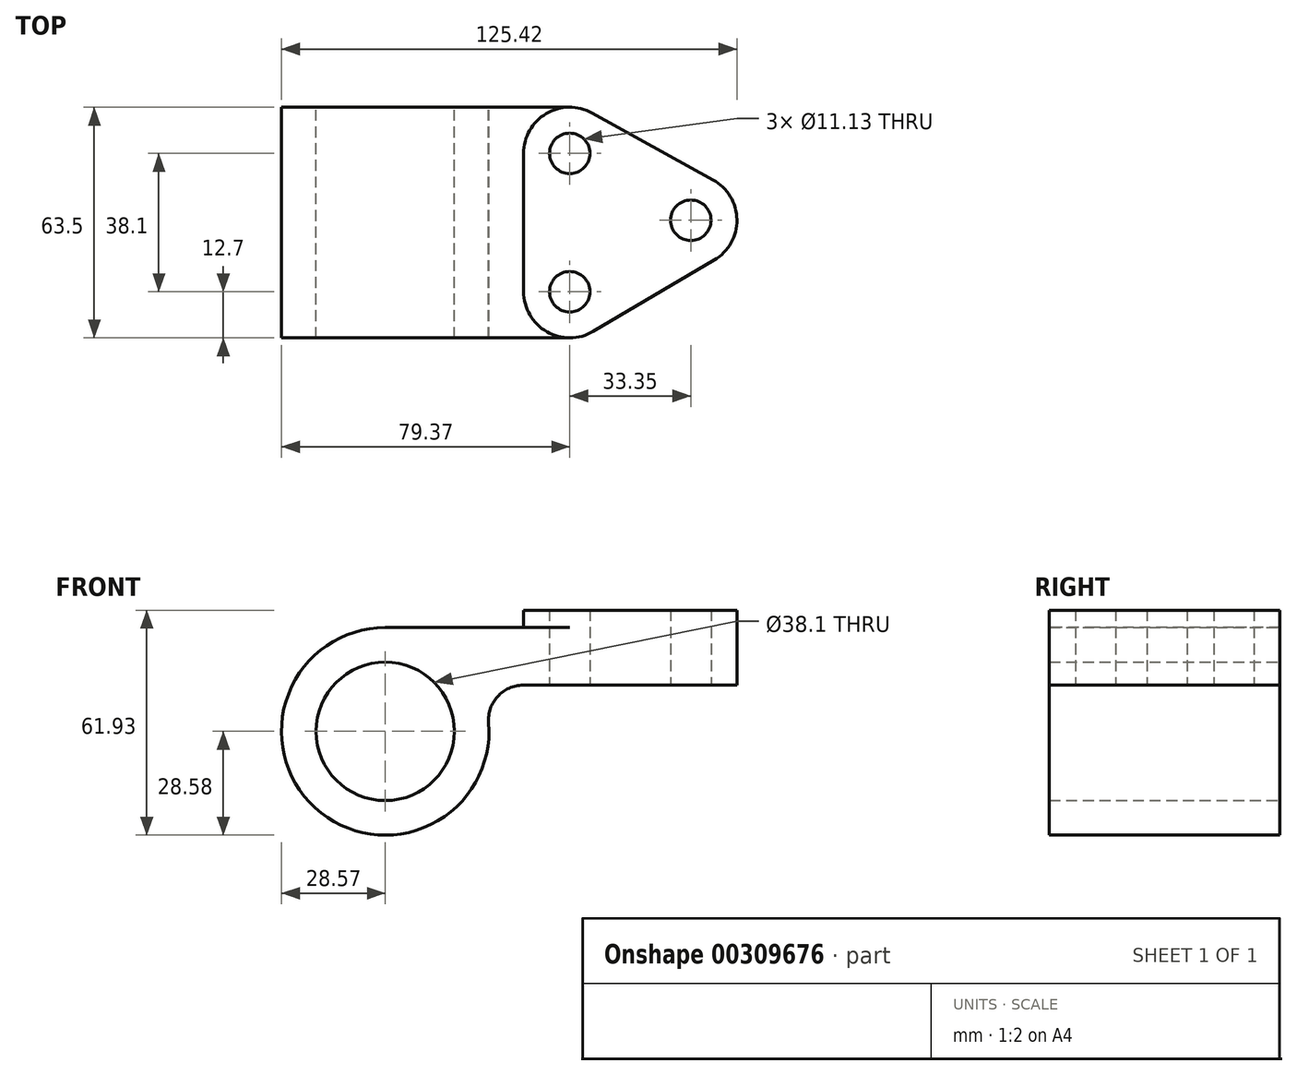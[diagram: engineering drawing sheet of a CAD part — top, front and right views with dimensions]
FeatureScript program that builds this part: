
annotation { "Feature Type Name" : "Feature", "Feature Type Description" : "" }
export const myFeature = defineFeature(function(context is Context, id is Id, definition is map)
    precondition{}
    {
        {
            var Q0;
            Q0=qCreatedBy(makeId("Front.planeOp"),FACE);
            var sketch = newSketch(context, id + "F0", { "sketchPlane" : qUnion([Q0])});
            skCircle(sketch, "E0", {"center": v(0, 0) * mm, "radius": 19.05 * mm});
            skLineSegment(sketch, "E1", {"start": v(0, 28.58) * mm, "end": v(139.57, 28.58) * mm});
            skLineSegment(sketch, "E2", {"start": v(139.57, 28.58) * mm, "end": v(139.57, 12.7) * mm});
            skLineSegment(sketch, "E3", {"start": v(139.57, 12.7) * mm, "end": v(37.97, 12.7) * mm});
            skArc(sketch, "E4", {"start": v(37.97, 12.7) * mm, "mid": v(30.96, 9.62) * mm, "end": v(28.48, 2.38) * mm});
            skArc(sketch, "E5", {"start": v(0, 28.58) * mm, "mid": v(-19.35, -21.03) * mm, "end": v(28.48, 2.38) * mm});
            skSolve(sketch);
        }
        {
            var Q0;
            Q0 = qSketchRegion(id + "F0", true);
            extrude(context, id + "F1", {"entities" : qUnion([Q0]), "endBound" : BoundingType.SYMMETRIC, "depth" : 63.5 * mm});
        }
        {
            var Q0;
            Q0=makeQuery(id+"F1.opExtrude","SWEPT_FACE",FACE,{"disambiguationData":[OSD([sQuery(id+"F0.wireOp",EDGE,"E1")])]});
            var sketch = newSketch(context, id + "F2", { "sketchPlane" : qUnion([Q0])});
            skLineSegment(sketch, "E6", {"start": v(38.1, 19.05) * mm, "end": v(38.1, -19.05) * mm});
            skArc(sketch, "E7", {"start": v(38.1, 19.05) * mm, "mid": v(44.35, 29.99) * mm, "end": v(56.94, 30.17) * mm});
            skArc(sketch, "E8", {"start": v(38.1, -19.05) * mm, "mid": v(44.5, -30.08) * mm, "end": v(57.25, -29.99) * mm});
            skLineSegment(sketch, "E9", {"start": v(56.94, 30.17) * mm, "end": v(90.3, 11.74) * mm});
            skLineSegment(sketch, "E10", {"start": v(57.25, -29.99) * mm, "end": v(90.6, -10.31) * mm});
            skArc(sketch, "E11", {"start": v(90.3, 11.74) * mm, "mid": v(96.85, 0.8) * mm, "end": v(90.6, -10.31) * mm});
            skCircle(sketch, "E12", {"center": v(50.8, 19.05) * mm, "radius": 5.56 * mm});
            skCircle(sketch, "E13", {"center": v(50.8, -19.05) * mm, "radius": 5.56 * mm});
            skCircle(sketch, "E14", {"center": v(84.15, 0.63) * mm, "radius": 5.56 * mm});
            skSolve(sketch);
        }
        {
            var Q0;
            Q0 = qSketchRegion(id + "F2", true);
            extrude(context, id + "F3", {"entities" : qUnion([Q0]), "operationType" : NewBodyOperationType.ADD, "depth" : 4.78 * mm});
        }
        {
            var Q0;
            Q0=makeQuery(id+"F3.boolean.opBoolean","SPLIT",FACE,{"disambiguationData":[TD([makeQuery(id+"F3.opExtrude","SWEPT_FACE",FACE,{"disambiguationData":[OSD([sQuery(id+"F2.wireOp",EDGE,"E12")])]})])],"derivedFrom":makeQuery(id+"F1.opExtrude","SWEPT_FACE",FACE,{"disambiguationData":[OSD([sQuery(id+"F0.wireOp",EDGE,"E1")])]})});
            var Q1;
            Q1=makeQuery(id+"F3.boolean.opBoolean","SPLIT",FACE,{"disambiguationData":[TD([makeQuery(id+"F3.opExtrude","SWEPT_FACE",FACE,{"disambiguationData":[OSD([sQuery(id+"F2.wireOp",EDGE,"E14")])]})])],"derivedFrom":makeQuery(id+"F1.opExtrude","SWEPT_FACE",FACE,{"disambiguationData":[OSD([sQuery(id+"F0.wireOp",EDGE,"E1")])]})});
            var Q2;
            Q2=makeQuery(id+"F3.boolean.opBoolean","SPLIT",FACE,{"disambiguationData":[TD([makeQuery(id+"F3.opExtrude","SWEPT_FACE",FACE,{"disambiguationData":[OSD([sQuery(id+"F2.wireOp",EDGE,"E13")])]})])],"derivedFrom":makeQuery(id+"F1.opExtrude","SWEPT_FACE",FACE,{"disambiguationData":[OSD([sQuery(id+"F0.wireOp",EDGE,"E1")])]})});
            var Q3;
            {var subQ0=sQuery(id+"F0.wireOp",EDGE,"E2");var subQ1=sQuery(id+"F0.wireOp",EDGE,"E1");var subQ2=makeQuery(id+"F1.opExtrude","SWEPT_FACE",FACE,{"disambiguationData":[OSD([subQ1])]});Q3=makeQuery(id+"F3.boolean.opBoolean","SPLIT",FACE,{"disambiguationData":[TD([makeQuery(id+"F1.opExtrude","SWEPT_FACE",FACE,{"disambiguationData":[OSD([subQ0])]})])],"derivedFrom":subQ2});}
            extrude(context, id + "F4", {"entities" : qUnion([Q0, Q1, Q2, Q3]), "operationType" : NewBodyOperationType.REMOVE, "endBound" : BoundingType.THROUGH_ALL, "oppositeDirection" : true, "depth" : 25.4 * mm});
        }
    });
